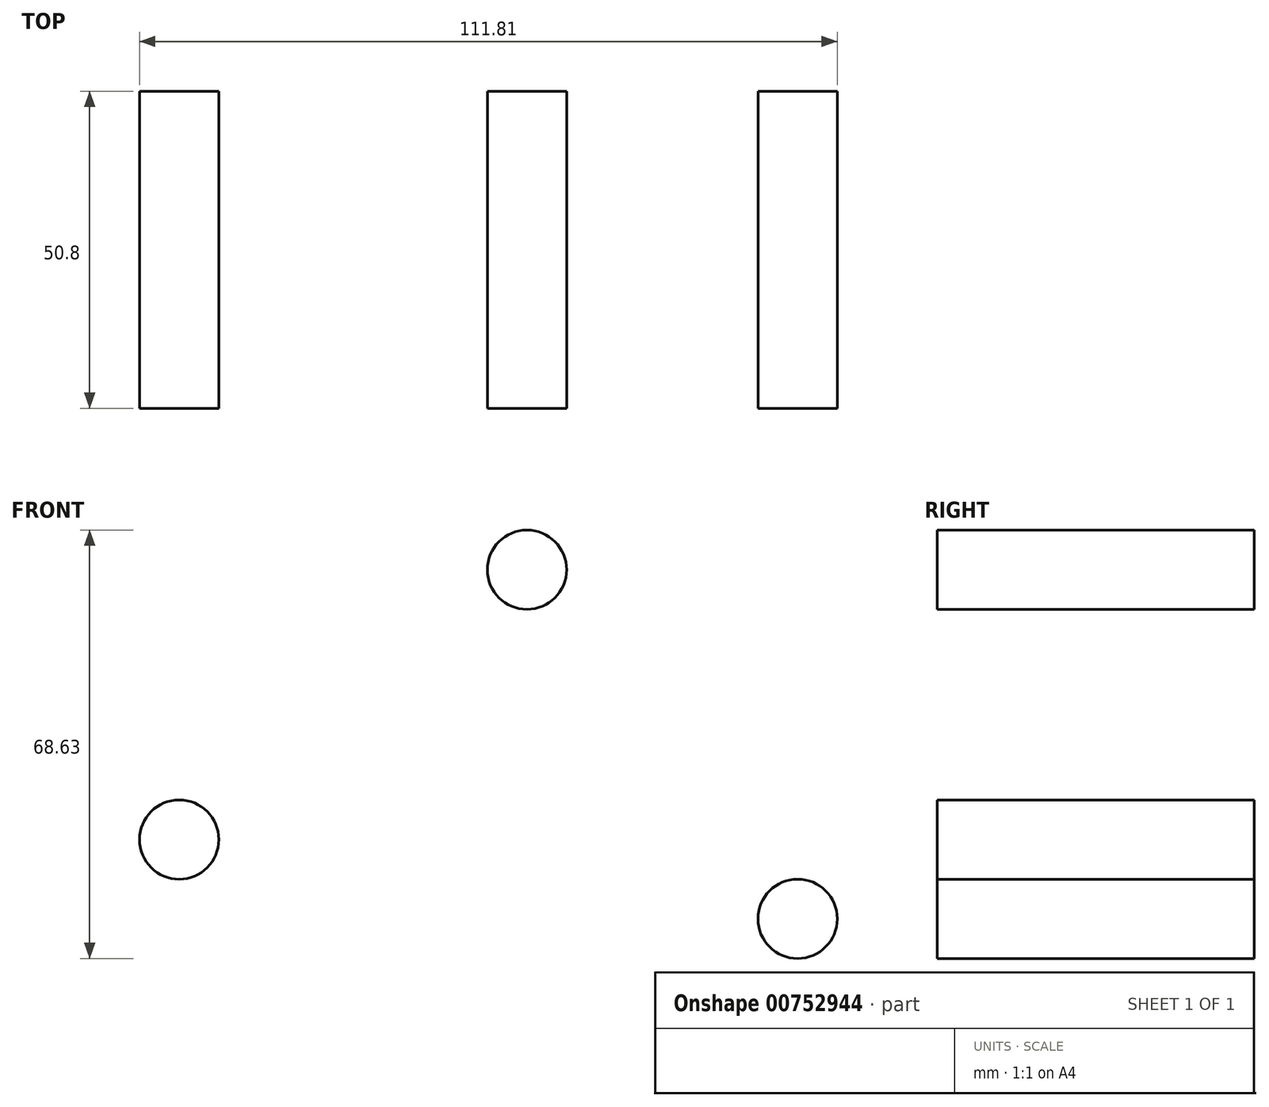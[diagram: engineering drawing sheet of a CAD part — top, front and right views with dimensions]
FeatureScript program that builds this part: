
annotation { "Feature Type Name" : "Feature", "Feature Type Description" : "" }
export const myFeature = defineFeature(function(context is Context, id is Id, definition is map)
    precondition{}
    {
        {
            var Q0;
            Q0=qCreatedBy(makeId("Front.planeOp"),FACE);
            var sketch = newSketch(context, id + "F0", { "sketchPlane" : qUnion([Q0])});
            skCircle(sketch, "E0", {"center": v(0, 0) * mm, "radius": 6.35 * mm});
            skLineSegment(sketch, "E1", {"start": v(0, -6.35) * mm, "end": v(49.55, -6.35) * mm, "construction": true});
            skLineSegment(sketch, "E2", {"start": v(49.55, -6.35) * mm, "end": v(49.55, -77.62) * mm, "construction": true});
            skLineSegment(sketch, "E3.MirrorCS", {"start": v(49.55, -6.35) * mm, "end": v(49.55, 64.92) * mm, "construction": true});
            skCircle(sketch, "E4.MirrorC", {"center": v(0, -12.7) * mm, "radius": 6.35 * mm});
            skCircle(sketch, "E5.MirrorC", {"center": v(99.1, -12.7) * mm, "radius": 6.35 * mm});
            skCircle(sketch, "E6.MirrorC", {"center": v(99.1, 0) * mm, "radius": 6.35 * mm});
            skLineSegment(sketch, "E7", {"start": v(49.55, -6.35) * mm, "end": v(-19.77, -75.91) * mm, "construction": true});
            skCircle(sketch, "E8.MirrorC", {"center": v(56.07, -55.88) * mm, "radius": 6.35 * mm});
            skCircle(sketch, "E9.MirrorC", {"center": v(55.74, 43.23) * mm, "radius": 6.35 * mm});
            skSolve(sketch);
        }
        {
            var Q0;
            Q0=makeQuery(id+"F0.imprint","IMPRINT",FACE,{"disambiguationData":[TD([[makeQuery(id+"F0.imprint","IMPRINT",EDGE,{"derivedFrom":sQuery(id+"F0.wireOp",EDGE,"E0")}),1.0]])]});
            var Q1;
            Q1=makeQuery(id+"F0.imprint","IMPRINT",FACE,{"disambiguationData":[TD([[makeQuery(id+"F0.imprint","IMPRINT",EDGE,{"derivedFrom":sQuery(id+"F0.wireOp",EDGE,"E4.MirrorC")}),-1.0]])]});
            var Q2;
            Q2=makeQuery(id+"F0.imprint","IMPRINT",FACE,{"disambiguationData":[TD([[makeQuery(id+"F0.imprint","IMPRINT",EDGE,{"derivedFrom":sQuery(id+"F0.wireOp",EDGE,"E8.MirrorC")}),-1.0]])]});
            var Q3;
            Q3=makeQuery(id+"F0.imprint","IMPRINT",FACE,{"disambiguationData":[TD([[makeQuery(id+"F0.imprint","IMPRINT",EDGE,{"derivedFrom":sQuery(id+"F0.wireOp",EDGE,"E5.MirrorC")}),1.0]])]});
            var Q4;
            Q4=makeQuery(id+"F0.imprint","IMPRINT",FACE,{"disambiguationData":[TD([[makeQuery(id+"F0.imprint","IMPRINT",EDGE,{"derivedFrom":sQuery(id+"F0.wireOp",EDGE,"E6.MirrorC")}),-1.0]])]});
            var Q5;
            Q5=makeQuery(id+"F0.imprint","IMPRINT",FACE,{"disambiguationData":[TD([[makeQuery(id+"F0.imprint","IMPRINT",EDGE,{"derivedFrom":sQuery(id+"F0.wireOp",EDGE,"E9.MirrorC")}),1.0]])]});
            extrude(context, id + "F1", {"entities" : qUnion([Q0, Q1, Q2, Q3, Q4, Q5]), "depth" : 50.8 * mm, "offsetDistance" : 25.4 * mm, "symmetric" : true});
        }
    });
